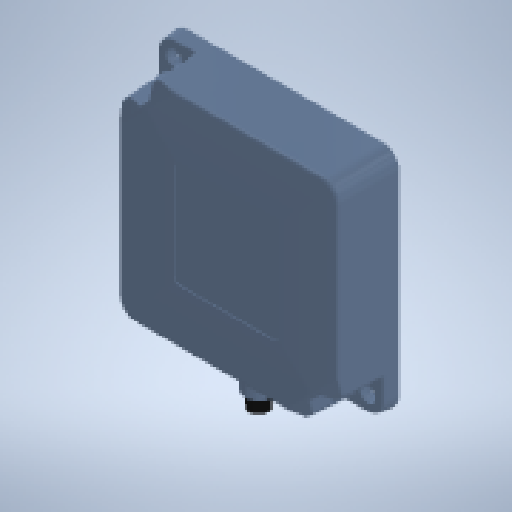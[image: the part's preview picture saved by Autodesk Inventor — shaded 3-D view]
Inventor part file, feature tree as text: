
AUTODESK INVENTOR PART (.ipt)
format: ipt  version: 2023 (Build 270158000, 158)  size: 739,840 bytes
history: native  units: in
note: dims shown in document units (in); Inventor stores cm internally (conversion verified against a paired STEP export)
features: extrude x2, sketch x2, other x1
ambient origin geometry x8: Origin, YZ Plane, XZ Plane, XY Plane, X Axis, Y Axis, Z Axis, Center Point
bodies: Solid1 (feature_tree)
feature tree (5):
  extrude  "Extrusion1"  TaperAngle=0.0deg  [1 undecoded]
  extrude  "Extrusion2"  [1 undecoded]
  sketch  "Sketch1"  dims[d0=3.3563in d1=0.0in d2=0.0in d3=0.0in]
  sketch  "Sketch2"
  parser-record x1  (decoder bookkeeping rows leaked as tree rows — omitted from the tree; the rows remain in map.json)
note: 2 required parameter values undecoded (feature->parameter linkage not recoverable at this tier; creation-order binding heuristic only, values carry confidence <= 0.55)
